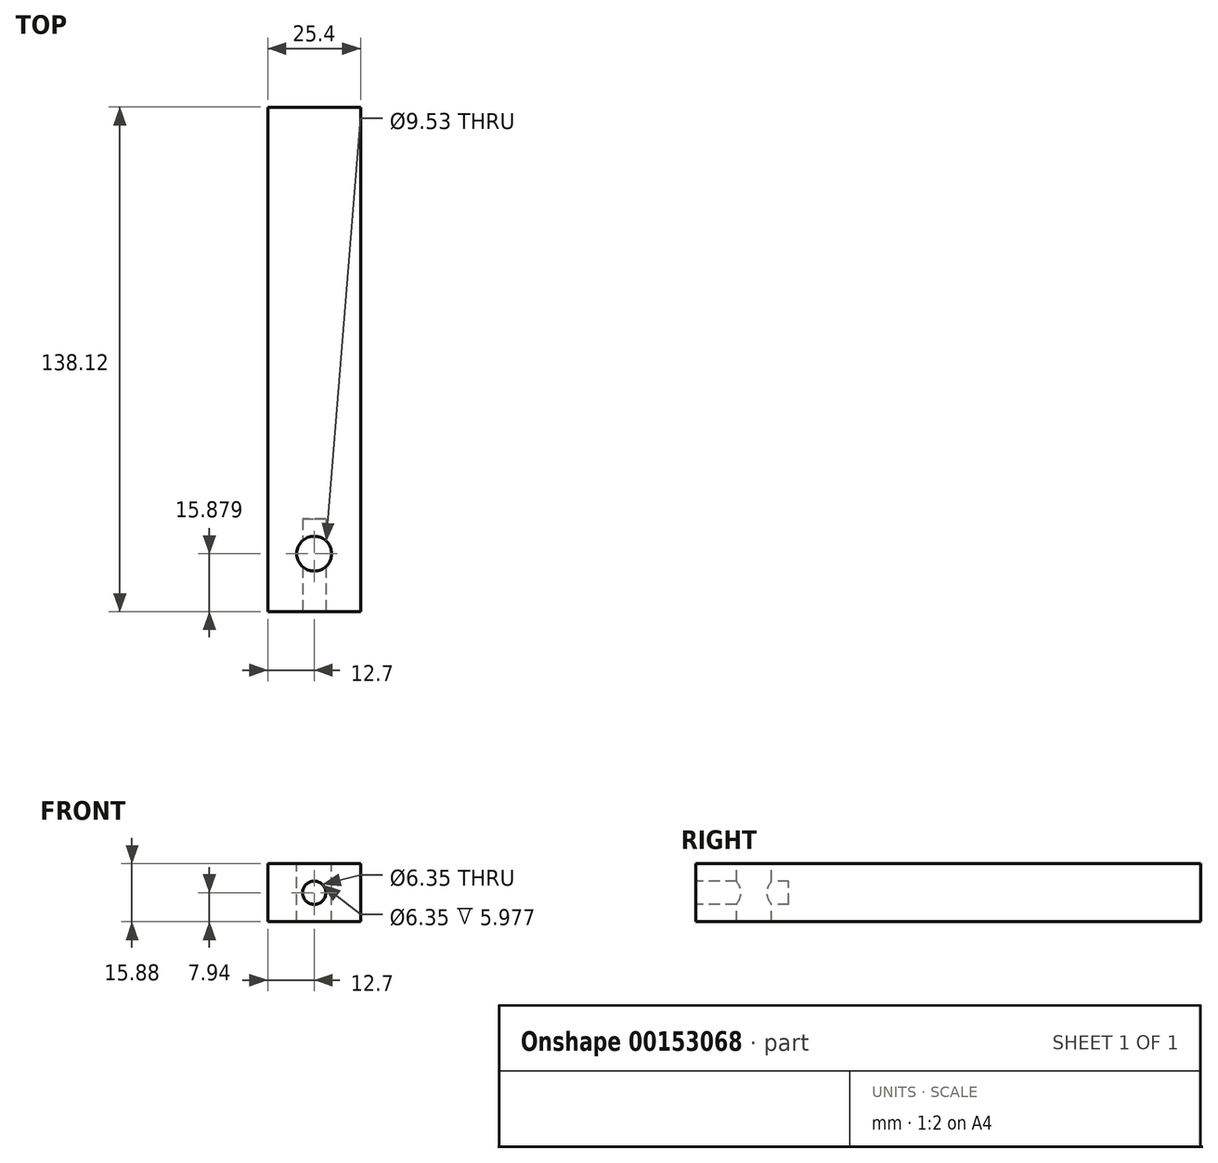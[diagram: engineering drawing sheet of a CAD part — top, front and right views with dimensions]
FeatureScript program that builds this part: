
annotation { "Feature Type Name" : "Feature", "Feature Type Description" : "" }
export const myFeature = defineFeature(function(context is Context, id is Id, definition is map)
    precondition{}
    {
        {
            var Q0;
            Q0=qCreatedBy(makeId("Front.planeOp"),FACE);
            var sketch = newSketch(context, id + "F0", { "sketchPlane" : qUnion([Q0])});
            skLineSegment(sketch, "E0.bottom", {"start": v(12.7, -7.94) * mm, "end": v(-12.7, -7.94) * mm});
            skLineSegment(sketch, "E0.top", {"start": v(12.7, 7.94) * mm, "end": v(-12.7, 7.94) * mm});
            skLineSegment(sketch, "E0.left", {"start": v(12.7, -7.94) * mm, "end": v(12.7, 7.94) * mm});
            skLineSegment(sketch, "E0.right", {"start": v(-12.7, -7.94) * mm, "end": v(-12.7, 7.94) * mm});
            skPoint(sketch, "E0.middle", {"position": v(0, 0) * mm});
            skSolve(sketch);
        }
        {
            var Q0;
            Q0 = qSketchRegion(id + "F0", true);
            extrude(context, id + "F1", {"entities" : qUnion([Q0]), "oppositeDirection" : true, "depth" : 69.06 * mm, "hasSecondDirection" : true, "secondDirectionOppositeDirection" : false, "secondDirectionDepth" : 69.06 * mm});
        }
        {
            var Q0;
            Q0=makeQuery(id+"F1.opExtrude","SWEPT_FACE",FACE,{"disambiguationData":[OSD([sQuery(id+"F0.wireOp",EDGE,"E0.top")])]});
            var sketch = newSketch(context, id + "F2", { "sketchPlane" : qUnion([Q0])});
            skCircle(sketch, "E1", {"center": v(0, -53.18) * mm, "radius": 4.76 * mm});
            skPoint(sketch, "E1.centerSnap0", {"position": v(0, -69.06) * mm});
            skSolve(sketch);
        }
        {
            var Q0;
            Q0 = qSketchRegion(id + "F2", true);
            extrude(context, id + "F3", {"entities" : qUnion([Q0]), "operationType" : NewBodyOperationType.REMOVE, "endBound" : BoundingType.THROUGH_ALL, "oppositeDirection" : true, "depth" : 25.4 * mm});
        }
        {
            var Q0;
            Q0=makeQuery(id+"F1.opExtrude","CAP_FACE",FACE,{"disambiguationData":[OSD([sQuery(id+"F0.wireOp",EDGE,"E0.bottom"),sQuery(id+"F0.wireOp",EDGE,"E0.top"),sQuery(id+"F0.wireOp",EDGE,"E0.left"),sQuery(id+"F0.wireOp",EDGE,"E0.right")])],"isStart":true});
            var sketch = newSketch(context, id + "F4", { "sketchPlane" : qUnion([Q0])});
            skCircle(sketch, "E2", {"center": v(0, 0) * mm, "radius": 3.18 * mm});
            skSolve(sketch);
        }
        {
            var Q0;
            Q0 = qSketchRegion(id + "F4", true);
            extrude(context, id + "F5", {"entities" : qUnion([Q0]), "operationType" : NewBodyOperationType.REMOVE, "oppositeDirection" : true, "depth" : 25.4 * mm});
        }
    });
